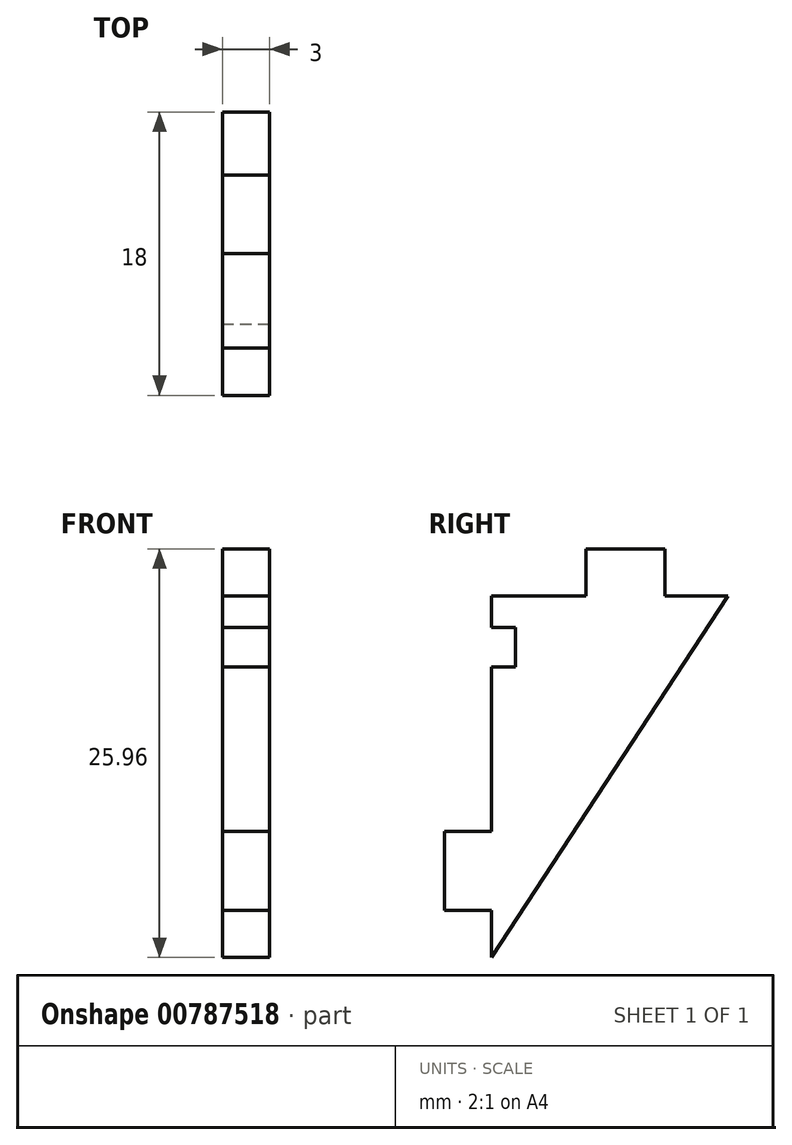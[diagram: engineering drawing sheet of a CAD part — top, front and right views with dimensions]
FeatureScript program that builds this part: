
annotation { "Feature Type Name" : "Feature", "Feature Type Description" : "" }
export const myFeature = defineFeature(function(context is Context, id is Id, definition is map)
    precondition{}
    {
        {
            var Q0;
            Q0=qCreatedBy(makeId("Right.planeOp"),FACE);
            var sketch = newSketch(context, id + "F0", { "sketchPlane" : qUnion([Q0])});
            skLineSegment(sketch, "E0", {"start": v(-7.88, 26.73) * mm, "end": v(-1.88, 26.73) * mm});
            skLineSegment(sketch, "E1", {"start": v(7.12, 26.73) * mm, "end": v(-7.88, 3.77) * mm});
            skLineSegment(sketch, "E2", {"start": v(-7.88, 3.77) * mm, "end": v(-7.88, 6.77) * mm});
            skLineSegment(sketch, "E3.top", {"start": v(3.12, 29.73) * mm, "end": v(-1.88, 29.73) * mm});
            skLineSegment(sketch, "E3.left", {"start": v(-1.88, 26.73) * mm, "end": v(-1.88, 29.73) * mm});
            skLineSegment(sketch, "E3.right", {"start": v(3.12, 26.73) * mm, "end": v(3.12, 29.73) * mm});
            skLineSegment(sketch, "E4.bottom", {"start": v(-7.88, 11.77) * mm, "end": v(-10.88, 11.77) * mm});
            skLineSegment(sketch, "E4.top", {"start": v(-7.88, 6.77) * mm, "end": v(-10.88, 6.77) * mm});
            skLineSegment(sketch, "E4.right", {"start": v(-10.88, 11.77) * mm, "end": v(-10.88, 6.77) * mm});
            skPoint(sketch, "E5", {"position": v(0.62, 26.73) * mm});
            skLineSegment(sketch, "E6", {"start": v(-7.88, 24.73) * mm, "end": v(-6.38, 24.73) * mm});
            skLineSegment(sketch, "E7", {"start": v(-6.38, 24.73) * mm, "end": v(-6.38, 22.23) * mm});
            skLineSegment(sketch, "E8", {"start": v(-6.38, 22.23) * mm, "end": v(-7.88, 22.23) * mm});
            skLineSegment(sketch, "E9.trimOffspring", {"start": v(-7.88, 11.77) * mm, "end": v(-7.88, 22.23) * mm});
            skLineSegment(sketch, "E10.trimOffspring", {"start": v(3.12, 26.73) * mm, "end": v(7.12, 26.73) * mm});
            skLineSegment(sketch, "E11", {"start": v(-7.88, 26.73) * mm, "end": v(-7.88, 24.73) * mm});
            skSolve(sketch);
        }
        {
            var Q0;
            {var subQ1=sQuery(id+"F0.wireOp",EDGE,"E1");Q0=makeQuery(id+"F0.imprint","IMPRINT",FACE,{"disambiguationData":[TD([[makeQuery(id+"F0.imprint","IMPRINT",EDGE,{"derivedFrom":subQ1}),-1.0]])]});}
            var Q1;
            Q1=makeQuery(id+"F0.imprint","IMPRINT",FACE,{"disambiguationData":[TD([[makeQuery(id+"F0.imprint","IMPRINT",EDGE,{"derivedFrom":sQuery(id+"F0.wireOp",EDGE,"E3.bottom")}),-1.0]])]});
            var Q2;
            Q2=makeQuery(id+"F0.imprint","IMPRINT",FACE,{"disambiguationData":[TD([[makeQuery(id+"F0.imprint","IMPRINT",EDGE,{"derivedFrom":sQuery(id+"F0.wireOp",EDGE,"E4.bottom")}),1.0]])]});
            extrude(context, id + "F1", {"entities" : qUnion([Q0, Q1, Q2]), "depth" : 3 * mm, "offsetDistance" : 25.4 * mm});
        }
    });
